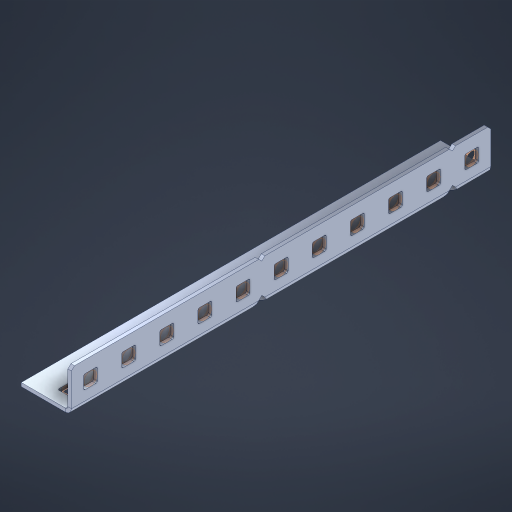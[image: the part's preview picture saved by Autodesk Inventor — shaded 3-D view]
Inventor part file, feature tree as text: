
AUTODESK INVENTOR PART (.ipt)
format: ipt  version: 2023 (Build 270158000, 158)  size: 584,704 bytes
history: native  units: in
note: dims shown in document units (in); Inventor stores cm internally (conversion verified against a paired STEP export)
features: other x27, extrude x21, sheet_metal_op x10, sketch x8, mirror x1, pattern_linear x1, chamfer x1
ambient origin geometry x8: Origin, YZ Plane, XZ Plane, XY Plane, X Axis, Y Axis, Z Axis, Center Point
bodies: Solid1 (feature_tree), Body (feature_tree)
feature tree (69):
  other  "Flange Pattern Plane"
  sheet_metal_op  "Flange Pattern"
  sheet_metal_op  "Body Pattern"
  other  "Arc Length"
  mirror  "Notch Mirror"
  pattern_linear  "Notch Pattern"  Spacing1=0.1875in  [1 undecoded]
  chamfer  "End Chamfer"
  extrude  "Half Cut"  Depth=0.0469in
  sketch  "Sketch1"  dims[d0=2.5in]
  other  "Plate1"
  sketch  "Sketch2"  dims[d1=5.5in]
  other  "Plate2"
  sheet_metal_op  "Bend1"
  sheet_metal_op  "Corner1"
  sketch  "Sketch3"  dims[d2=0.0469in]
  other  "Flange Pattern Sketch"
  sketch  "Sketch7"  dims[d3=0.0469in]
  other  "Srf1"
  other  "Srf2"
  sketch  "Sketch8"  dims[d4=0.0234in]
  sketch  "Sketch9"  dims[d5=0.0938in]
  other  "Srf91"
  sheet_metal_op  "Body Pattern Sketch"
  other  "Srf92"
  sketch  "Sketch13"  dims[d6=0.0469in]
  sketch  "Sketch14"  dims[d7=0.5in d8=90.0deg d9=0.0312in d10=0.1875in d11=0.0469in d12=0.0469in d16=0.182in d17=0.02in d18=0.0469in d19=0.0in d20=0.25in d21=0.25in d46=0.172in d47=1.0in d48=0.0in d49=0.182in d50=0.02in d51=0.25in d52=0.25in d53=0.0469in d54=0.0in d55=0.172in d56=1.0in d57=0.0in d60=4.3307in d62=0.5in d63=0.3937in d65=0.5in d85=0.1227in d86=0.1659in d88=0.04in d89=0.0469in d90=0.0in d91=0.04in d92=0.0491in d95=2.5in d96=0.04in d97=0.25in d98=45.0deg d101=0.0in d102=2.497in d131=0.5in d132=4.3307in d134=0.5in d139=0.5in]
  other  "Srf856"
  other  "Srf1310"
  other  "Srf1311"
  other  "Srf1312"
  other  "Srf1376"
  other  "Srf1377"
  other  "Srf1728"
  other  "Srf1755"
  other  "Srf1878"
  other  "Srf1879"
  other  "Srf1880"
  other  "Srf1881"
  other  "Srf1882"
  other  "Srf1942"
  other  "Srf1943"
  other  "Srf1944"
  other  "Srf1945"
  other  "Srf1946"
  sheet_metal_op  "Flange Stamp"
  sheet_metal_op  "Flange Circle"
  sheet_metal_op  "Body Stamp"
  sheet_metal_op  "Body Circle"
  sheet_metal_op  "Notch"
  extrude  "ExtrusionSrf2"  Depth=0.0469in
  extrude  "ExtrusionSrf92"  Depth=0.5in
  extrude  "ExtrusionSrf856"  Depth=0.02in
  extrude  "ExtrusionSrf1310"  Depth=0.0469in
  extrude  "ExtrusionSrf1311"  TaperAngle=0.0deg  [1 undecoded]
  extrude  "ExtrusionSrf1312"  Depth=0.5in
  extrude  "ExtrusionSrf1376"  Depth=0.5in
  extrude  "ExtrusionSrf1377"  Depth=0.5in
  extrude  "ExtrusionSrf1728"  Depth=0.5in TaperAngle=0.0deg
  extrude  "ExtrusionSrf1755"  Depth=0.5in
  extrude  "ExtrusionSrf1878"  Depth=0.02in
  extrude  "ExtrusionSrf1879"  Depth=0.5in
  extrude  "ExtrusionSrf1880"  Depth=0.5in
  extrude  "ExtrusionSrf1881"  Depth=0.0469in
  extrude  "ExtrusionSrf1882"  TaperAngle=0.0deg  [1 undecoded]
  extrude  "ExtrusionSrf1942"  Depth=0.5in
  extrude  "ExtrusionSrf1943"  Depth=0.5in TaperAngle=0.0deg
  extrude  "ExtrusionSrf1944"  Depth=0.5in
  extrude  "ExtrusionSrf1945"  Depth=0.5in
  extrude  "ExtrusionSrf1946"  Depth=0.5in
note: 3 required parameter values undecoded (feature->parameter linkage not recoverable at this tier; creation-order binding heuristic only, values carry confidence <= 0.55)
